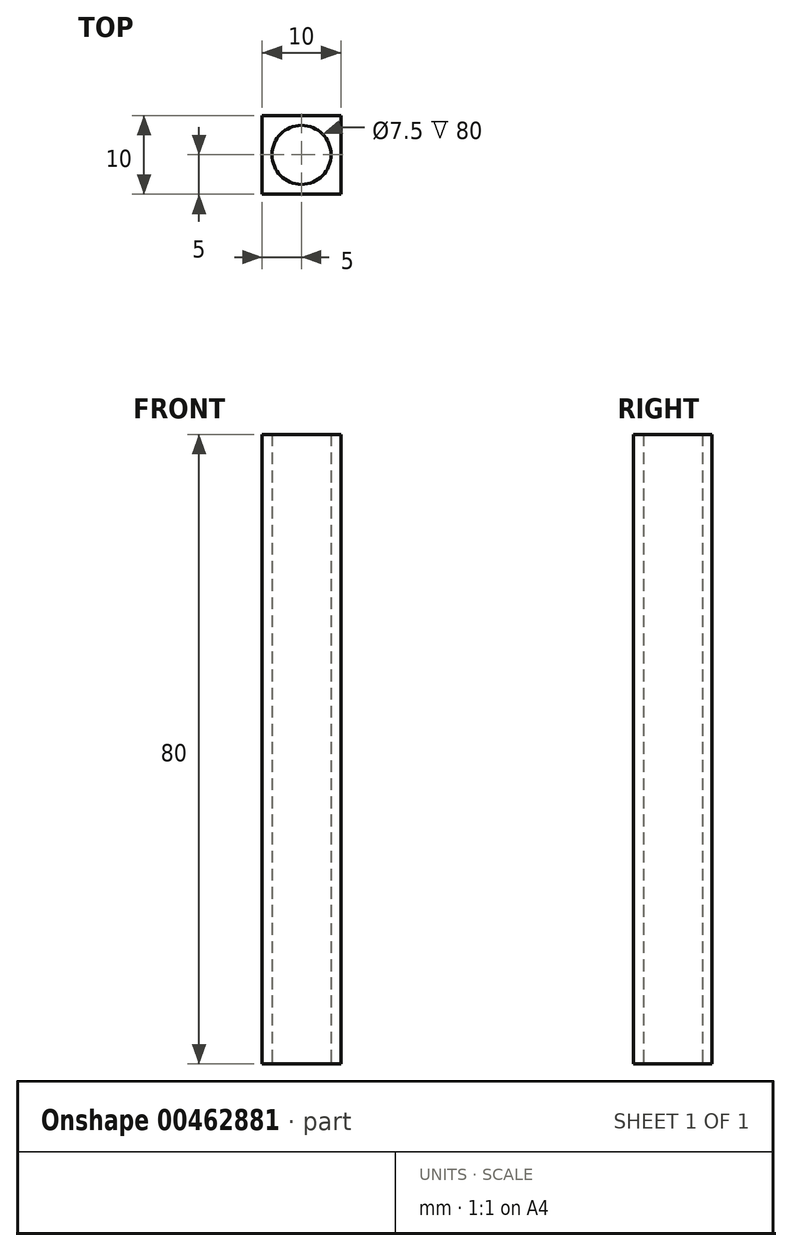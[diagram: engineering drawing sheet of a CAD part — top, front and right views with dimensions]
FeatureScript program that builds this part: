
annotation { "Feature Type Name" : "Feature", "Feature Type Description" : "" }
export const myFeature = defineFeature(function(context is Context, id is Id, definition is map)
    precondition{}
    {
        {
            var Q0;
            Q0=qCreatedBy(makeId("Top.planeOp"),FACE);
            var sketch = newSketch(context, id + "F0", { "sketchPlane" : qUnion([Q0])});
            skLineSegment(sketch, "E0.bottom", {"start": v(-5, 5) * mm, "end": v(5, 5) * mm});
            skLineSegment(sketch, "E0.top", {"start": v(-5, -5) * mm, "end": v(5, -5) * mm});
            skLineSegment(sketch, "E0.left", {"start": v(-5, 5) * mm, "end": v(-5, -5) * mm});
            skLineSegment(sketch, "E0.right", {"start": v(5, 5) * mm, "end": v(5, -5) * mm});
            skPoint(sketch, "E0.middle", {"position": v(0, 0) * mm});
            skCircle(sketch, "E1", {"center": v(0, 0) * mm, "radius": 3.75 * mm});
            skSolve(sketch);
        }
        {
            var Q0;
            Q0=qSketchRegion(id+"F0",true);
            extrude(context, id + "F1", {"entities" : qUnion([Q0]), "depth" : 70 * mm});
        }
        {
            var Q0;
            Q0=makeQuery(id+"F1.opExtrude","CAP_FACE",FACE,{"disambiguationData":[OSD([sQuery(id+"F0.wireOp",EDGE,"E0.bottom"),sQuery(id+"F0.wireOp",EDGE,"E0.top"),sQuery(id+"F0.wireOp",EDGE,"E0.left"),sQuery(id+"F0.wireOp",EDGE,"E0.right"),sQuery(id+"F0.wireOp",EDGE,"E1")])],"isStart":false});
            extrude(context, id + "F2", {"entities" : qUnion([Q0]), "operationType" : NewBodyOperationType.ADD, "depth" : 10 * mm});
        }
    });
